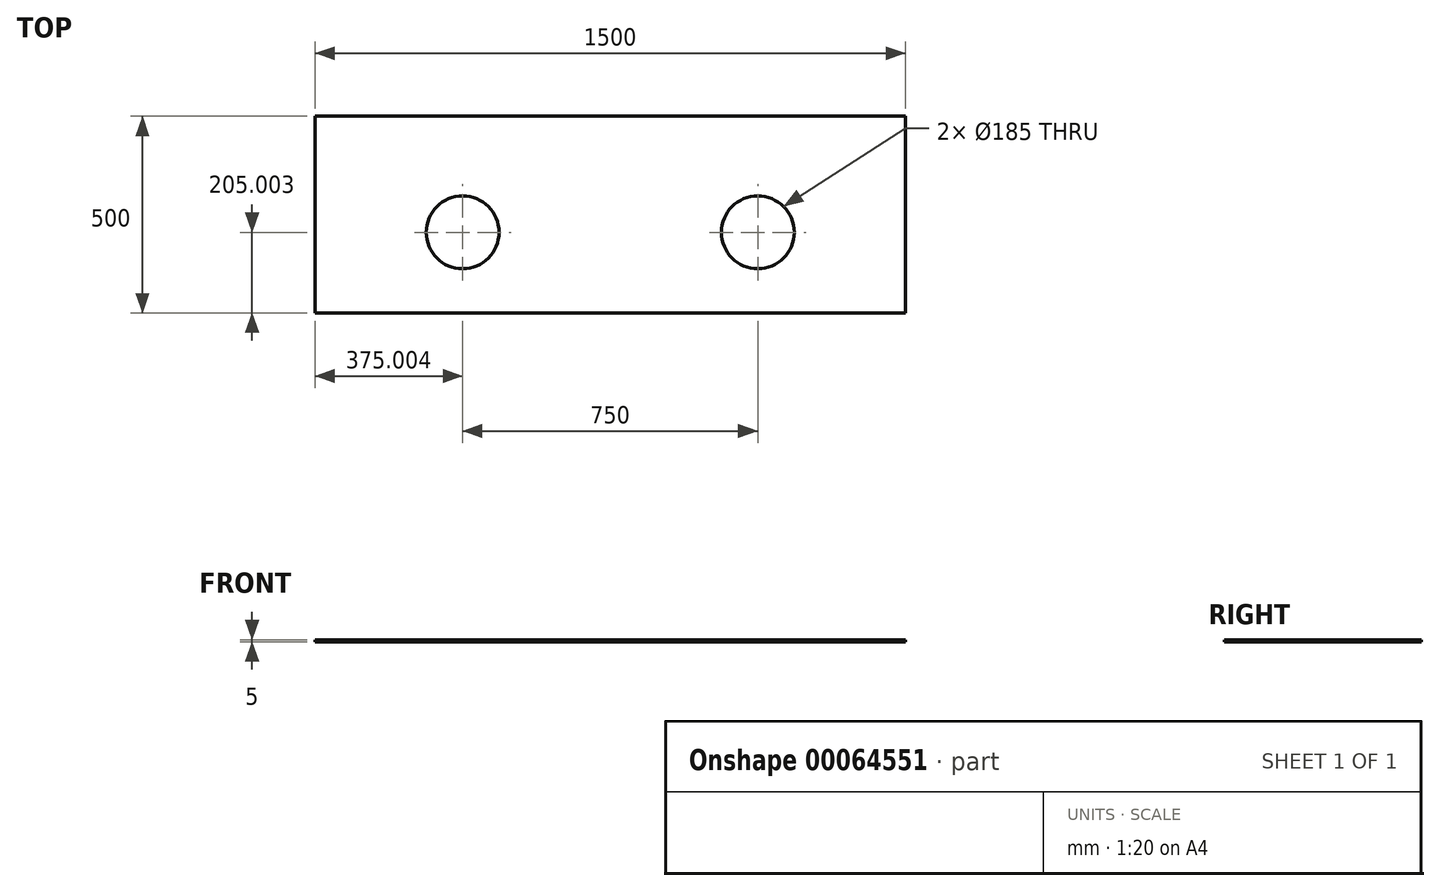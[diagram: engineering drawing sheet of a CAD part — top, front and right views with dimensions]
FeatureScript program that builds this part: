
annotation { "Feature Type Name" : "Feature", "Feature Type Description" : "" }
export const myFeature = defineFeature(function(context is Context, id is Id, definition is map)
    precondition{}
    {
        {
            var Q0;
            Q0=qCreatedBy(makeId("Top.planeOp"),FACE);
            var sketch = newSketch(context, id + "F0", { "sketchPlane" : qUnion([Q0])});
            skLineSegment(sketch, "E0.bottom", {"start": v(-813.83, 173.01) * mm, "end": v(686.17, 173.01) * mm});
            skLineSegment(sketch, "E0.top", {"start": v(-813.83, -326.99) * mm, "end": v(686.17, -326.99) * mm});
            skLineSegment(sketch, "E0.left", {"start": v(-813.83, 173.01) * mm, "end": v(-813.83, -326.99) * mm});
            skLineSegment(sketch, "E0.right", {"start": v(686.17, 173.01) * mm, "end": v(686.17, -326.99) * mm});
            skSolve(sketch);
        }
        {
            var Q0;
            Q0 = qSketchRegion(id + "F0", true);
            extrude(context, id + "F1", {"entities" : qUnion([Q0]), "depth" : 5 * mm});
        }
        {
            var Q0;
            Q0=makeQuery(id+"F1.opExtrude","CAP_FACE",FACE,{"disambiguationData":[OSD([sQuery(id+"F0.wireOp",EDGE,"E0.bottom"),sQuery(id+"F0.wireOp",EDGE,"E0.top"),sQuery(id+"F0.wireOp",EDGE,"E0.left"),sQuery(id+"F0.wireOp",EDGE,"E0.right")])],"isStart":false});
            var sketch = newSketch(context, id + "F2", { "sketchPlane" : qUnion([Q0])});
            skPoint(sketch, "E1", {"position": v(-438.83, -121.99) * mm});
            skPoint(sketch, "E2", {"position": v(311.17, -121.99) * mm});
            skSolve(sketch);
        }
        {
            var Q0;
            Q0=sQuery(id+"F2.wireOp",VERTEX,"E1");
            var Q1;
            Q1=sQuery(id+"F2.wireOp",VERTEX,"E2");
            var Q2;
            Q2=makeQuery(id+"F1.opExtrude","SWEPT_BODY",BODY,{"disambiguationData":[OSD([sQuery(id+"F0.wireOp",EDGE,"E0.bottom"),sQuery(id+"F0.wireOp",EDGE,"E0.top"),sQuery(id+"F0.wireOp",EDGE,"E0.left"),sQuery(id+"F0.wireOp",EDGE,"E0.right")])]});
            hole(context, id + "F3", {"style" : HoleStyle.SIMPLE, "holeDiameter" : 185 * mm, "endStyle" : HoleEndStyle.THROUGH, "locations" : qUnion([Q0, Q1]), "scope" : qUnion([Q2])});
        }
    });
